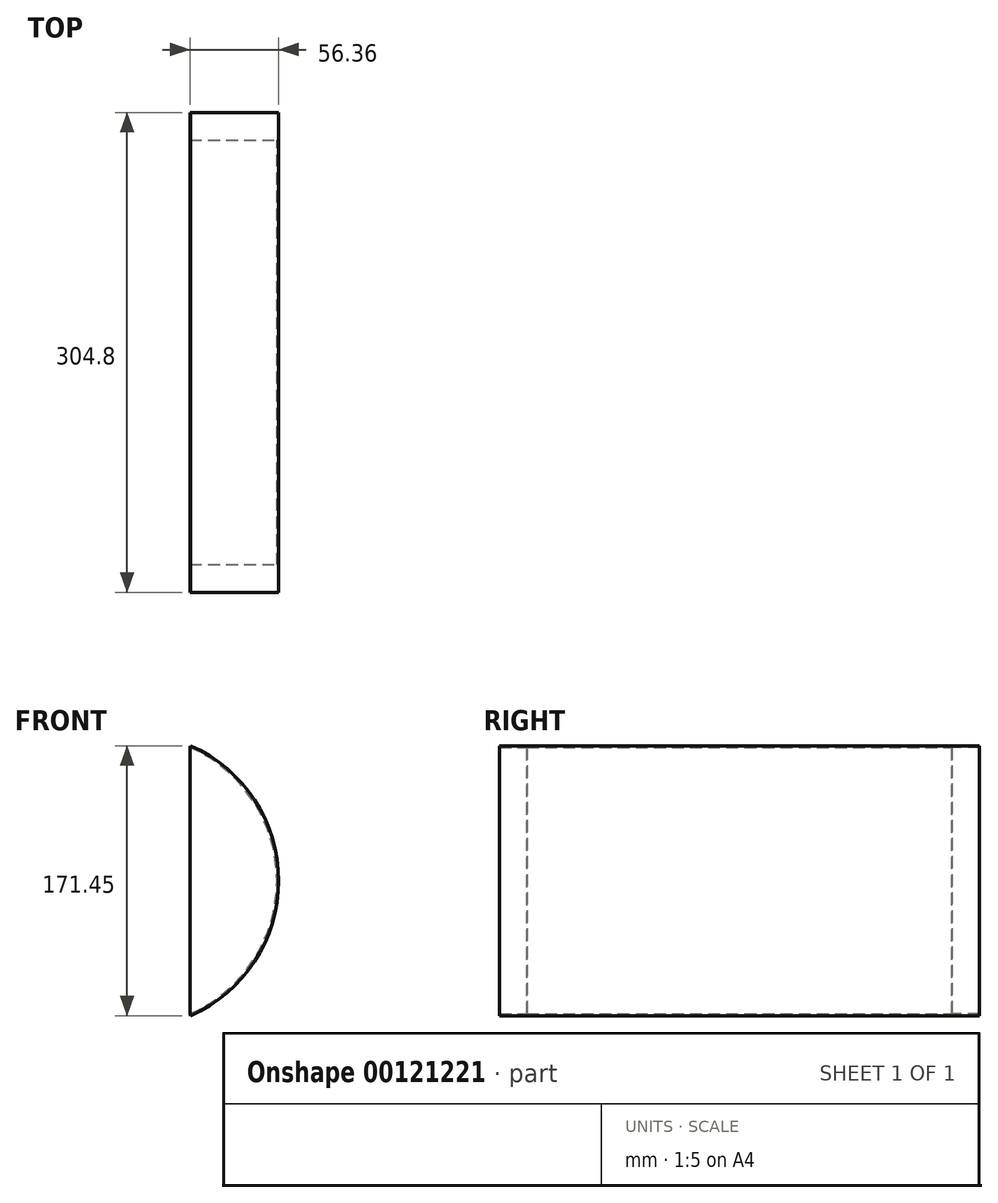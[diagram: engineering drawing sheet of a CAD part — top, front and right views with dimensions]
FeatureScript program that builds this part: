
annotation { "Feature Type Name" : "Feature", "Feature Type Description" : "" }
export const myFeature = defineFeature(function(context is Context, id is Id, definition is map)
    precondition{}
    {
        {
            var Q0;
            Q0=qCreatedBy(makeId("Front.planeOp"),FACE);
            var sketch = newSketch(context, id + "F0", { "sketchPlane" : qUnion([Q0])});
            skArc(sketch, "E0", {"start": v(0, -85.72) * mm, "mid": v(55.88, 0) * mm, "end": v(0, 85.73) * mm});
            skArc(sketch, "E1.0", {"start": v(-0.48, -84.64) * mm, "mid": v(54.7, 0) * mm, "end": v(-0.48, 84.64) * mm});
            skLineSegment(sketch, "E2", {"start": v(-0.48, 84.64) * mm, "end": v(0, 85.73) * mm});
            skLineSegment(sketch, "E3", {"start": v(-0.48, -84.64) * mm, "end": v(0, -85.72) * mm});
            skSolve(sketch);
        }
        {
            var Q0;
            Q0 = qSketchRegion(id + "F0", true);
            extrude(context, id + "F1", {"entities" : qUnion([Q0]), "endBound" : BoundingType.SYMMETRIC, "depth" : 304.8 * mm});
        }
        {
            var Q0;
            Q0=makeQuery(id+"F1.opExtrude","CAP_FACE",FACE,{"disambiguationData":[OSD([sQuery(id+"F0.wireOp",EDGE,"E0"),sQuery(id+"F0.wireOp",EDGE,"E1.0"),sQuery(id+"F0.wireOp",EDGE,"E2"),sQuery(id+"F0.wireOp",EDGE,"E3")])],"isStart":false});
            var sketch = newSketch(context, id + "F2", { "sketchPlane" : qUnion([Q0])});
            skArc(sketch, "E4.0", {"start": v(-0.48, -84.64) * mm, "mid": v(54.7, 0) * mm, "end": v(-0.48, 84.64) * mm});
            skLineSegment(sketch, "E5", {"start": v(-0.48, 84.64) * mm, "end": v(-0.48, -84.64) * mm});
            skSolve(sketch);
        }
        {
            var Q0;
            Q0 = qSketchRegion(id + "F2", true);
            extrude(context, id + "F3", {"entities" : qUnion([Q0]), "operationType" : NewBodyOperationType.ADD, "oppositeDirection" : true, "depth" : 17.53 * mm});
        }
        {
            var Q0;
            Q0=makeQuery(id+"F1.opExtrude","SWEPT_BODY",BODY,{"disambiguationData":[OSD([sQuery(id+"F0.wireOp",EDGE,"E0"),sQuery(id+"F0.wireOp",EDGE,"E1.0"),sQuery(id+"F0.wireOp",EDGE,"E2"),sQuery(id+"F0.wireOp",EDGE,"E3")])]});
            var Q1;
            Q1=qCreatedBy(makeId("Front.planeOp"),FACE);
            mirror(context, id + "F4", {"operationType" : NewBodyOperationType.ADD, "entities" : qUnion([Q0]), "mirrorPlane" : qUnion([Q1])});
        }
    });
